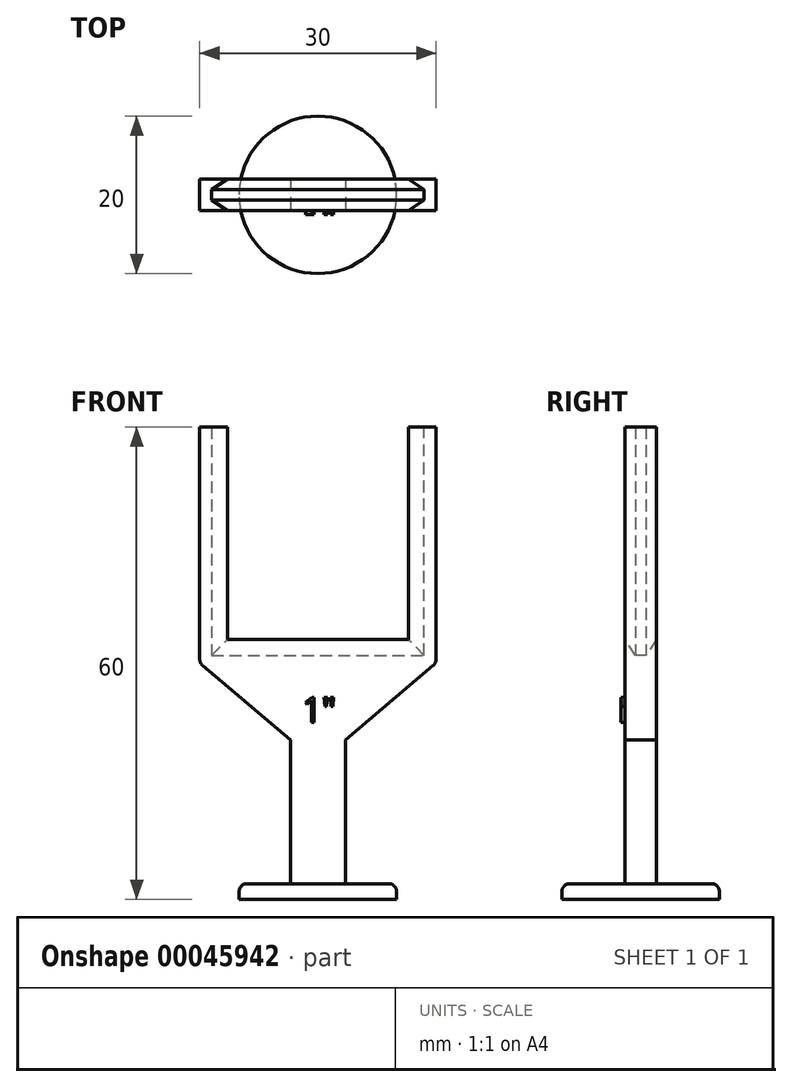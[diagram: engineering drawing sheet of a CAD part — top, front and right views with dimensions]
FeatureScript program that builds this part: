
annotation { "Feature Type Name" : "Feature", "Feature Type Description" : "" }
export const myFeature = defineFeature(function(context is Context, id is Id, definition is map)
    precondition{}
    {
        {
            var Q0;
            Q0=qCreatedBy(makeId("Top.planeOp"),FACE);
            var sketch = newSketch(context, id + "F0", { "sketchPlane" : qUnion([Q0])});
            skCircle(sketch, "E0", {"center": v(0, 0) * mm, "radius": 10 * mm});
            skSolve(sketch);
        }
        {
            var Q0;
            Q0=makeQuery(id+"F0.imprint","IMPRINT",FACE,{"disambiguationData":[TD([[makeQuery(id+"F0.imprint","IMPRINT",EDGE,{"derivedFrom":sQuery(id+"F0.wireOp",EDGE,"E0")}),1.0]])]});
            extrude(context, id + "F1", {"entities" : qUnion([Q0]), "depth" : 2 * mm});
        }
        {
            var Q0;
            Q0=qCreatedBy(makeId("Front.planeOp"),FACE);
            var sketch = newSketch(context, id + "F2", { "sketchPlane" : qUnion([Q0])});
            skLineSegment(sketch, "E1", {"start": v(0, 0) * mm, "end": v(0, 45) * mm, "construction": true});
            skLineSegment(sketch, "E2", {"start": v(-15, 45) * mm, "end": v(15, 45) * mm, "construction": true});
            skLineSegment(sketch, "E3", {"start": v(-3.5, 30) * mm, "end": v(3.5, 30) * mm, "construction": true});
            skLineSegment(sketch, "E4.0", {"start": v(-10, 2) * mm, "end": v(10, 2) * mm, "construction": true});
            skLineSegment(sketch, "E5", {"start": v(-3.5, 30) * mm, "end": v(-3.5, 2) * mm});
            skLineSegment(sketch, "E6.MirrorCS", {"start": v(3.5, 30) * mm, "end": v(3.5, 2) * mm});
            skLineSegment(sketch, "E7", {"start": v(-3.5, 2) * mm, "end": v(3.5, 2) * mm});
            skLineSegment(sketch, "E8.rect.bottom", {"start": v(15, 30) * mm, "end": v(-15, 30) * mm});
            skLineSegment(sketch, "E8.rect.top", {"start": v(15, 60) * mm, "end": v(-15, 60) * mm});
            skLineSegment(sketch, "E8.rect.left", {"start": v(15, 30) * mm, "end": v(15, 60) * mm});
            skLineSegment(sketch, "E8.rect.right", {"start": v(-15, 30) * mm, "end": v(-15, 60) * mm});
            skPoint(sketch, "E8.rect.middle", {"position": v(0, 45) * mm});
            skLineSegment(sketch, "E9.1", {"start": v(11.5, 33) * mm, "end": v(11.5, 60) * mm});
            skLineSegment(sketch, "E9.2", {"start": v(11.5, 33) * mm, "end": v(-11.5, 33) * mm});
            skLineSegment(sketch, "E9.3", {"start": v(-11.5, 33) * mm, "end": v(-11.5, 60) * mm});
            skLineSegment(sketch, "E10", {"start": v(0, 30) * mm, "end": v(0, 33) * mm, "construction": true});
            skLineSegment(sketch, "E11", {"start": v(0, 33) * mm, "end": v(-11.5, 33) * mm, "construction": true});
            skSolve(sketch);
        }
        {
            var Q0;
            {var subQ2=sQuery(id+"F2.wireOp",EDGE,"E5");Q0=makeQuery(id+"F2.imprint","IMPRINT",FACE,{"disambiguationData":[TD([[makeQuery(id+"F2.imprint","IMPRINT",EDGE,{"derivedFrom":subQ2}),1.0]])]});}
            var Q1;
            {var subQ0=sQuery(id+"F2.wireOp",EDGE,"E8.rect.left");Q1=makeQuery(id+"F2.imprint","IMPRINT",FACE,{"disambiguationData":[TD([[makeQuery(id+"F2.imprint","IMPRINT",EDGE,{"derivedFrom":subQ0}),1.0]])]});}
            extrude(context, id + "F3", {"entities" : qUnion([Q0, Q1]), "operationType" : NewBodyOperationType.ADD, "endBound" : BoundingType.SYMMETRIC, "depth" : 4 * mm, "hasSecondDirection" : true, "secondDirectionOppositeDirection" : true, "secondDirectionDepth" : 1.5 * mm});
        }
        {
            var Q0;
            Q0=makeQuery(id+"F3.opExtrude","CAP_VERTEX",VERTEX,{"disambiguationData":[OSD([sQuery(id+"F2.wireOp",EDGE,"E8.rect.top"),sQuery(id+"F2.wireOp",EDGE,"E9.3")])],"isStart":false});
            var Q1;
            Q1=makeQuery(id+"F3.opExtrude","CAP_EDGE",EDGE,{"disambiguationData":[OSD([sQuery(id+"F2.wireOp",EDGE,"E9.3")])],"isStart":false});
            cPlane(context, id + "F4", {"entities" : qUnion([Q0, Q1]), "cplaneType" : CPlaneType.CURVE_POINT, "offset" : 150 * mm, "width" : 150 * mm, "height" : 150 * mm});
        }
        {
            var Q0;
            Q0=qCreatedBy(id+"F4.planeOp",FACE);
            var sketch = newSketch(context, id + "F5", { "sketchPlane" : qUnion([Q0])});
            skLineSegment(sketch, "E12.0", {"start": v(-11.5, 2) * mm, "end": v(-11.5, -2) * mm});
            skLineSegment(sketch, "E13", {"start": v(-11.5, 0) * mm, "end": v(-13.5, 0) * mm, "construction": true});
            skLineSegment(sketch, "E14", {"start": v(-13.5, 0.65) * mm, "end": v(-13.5, -0.65) * mm});
            skLineSegment(sketch, "E15", {"start": v(-13.5, 0.65) * mm, "end": v(-11.5, 2) * mm});
            skLineSegment(sketch, "E16", {"start": v(-13.5, -0.65) * mm, "end": v(-11.5, -2) * mm});
            skSolve(sketch);
        }
        {
            var Q0;
            Q0=makeQuery(id+"F5.imprint","IMPRINT",FACE,{"disambiguationData":[TD([[makeQuery(id+"F5.imprint","IMPRINT",EDGE,{"derivedFrom":sQuery(id+"F5.wireOp",EDGE,"E12.0")}),-1.0]])]});
            var Q1;
            Q1=makeQuery(id+"F3.opExtrude","CAP_EDGE",EDGE,{"disambiguationData":[OSD([sQuery(id+"F2.wireOp",EDGE,"E9.3")])],"isStart":false});
            var Q2;
            Q2=makeQuery(id+"F3.opExtrude","CAP_EDGE",EDGE,{"disambiguationData":[OSD([sQuery(id+"F2.wireOp",EDGE,"E9.2")])],"isStart":false});
            var Q3;
            Q3=makeQuery(id+"F3.opExtrude","CAP_EDGE",EDGE,{"disambiguationData":[OSD([sQuery(id+"F2.wireOp",EDGE,"E9.1")])],"isStart":false});
            sweep(context, id + "F6", {"operationType" : NewBodyOperationType.REMOVE, "profiles" : qUnion([Q0]), "path" : qUnion([Q1, Q2, Q3])});
        }
        {
            var Q0;
            Q0=makeQuery(id+"F3.opExtrude","CAP_FACE",FACE,{"disambiguationData":[OSD([sQuery(id+"F2.wireOp",EDGE,"2eedeef1-0c84-48b1-a1d1-fd58b4077060"),sQuery(id+"F2.wireOp",EDGE,"c229b6c5-89b8-4870-855e-fcb2bb86a88d0.MirrorCS"),sQuery(id+"F2.wireOp",EDGE,"76dde04b-6d6e-49cb-a3f0-9f61c5932c53"),sQuery(id+"F2.wireOp",EDGE,"ccce22a9-8801-460d-b2e6-72a3cf553eda"),sQuery(id+"F2.wireOp",EDGE,"E5"),sQuery(id+"F2.wireOp",EDGE,"E6.MirrorCS"),sQuery(id+"F2.wireOp",EDGE,"E7")])],"isStart":false});
            var sketch = newSketch(context, id + "F7", { "sketchPlane" : qUnion([Q0])});
            skText(sketch, "E17", { "text": "1\"", "fontName": "OpenSans-Regular.ttf"});
            skPoint(sketch, "E18.1", {"position": v(0, 0) * mm});
            skLineSegment(sketch, "E19.0", {"start": v(0, 0) * mm, "end": v(0, 45) * mm, "construction": true});
            const initialGuessF7  = {"E17": [-0.002, 0.0225, 1, 0, 0.00317]};
            skSetInitialGuess(sketch, initialGuessF7);
            skSolve(sketch);
        }
        {
            var Q0;
            Q0=qSketchRegion(id+"F7",true);
            extrude(context, id + "F8", {"entities" : qUnion([Q0]), "operationType" : NewBodyOperationType.ADD, "depth" : .5 * mm});
        }
        {
            var Q0;
            Q0=makeQuery(id+"F3.opExtrude","CAP_FACE",FACE,{"disambiguationData":[OSD([sQuery(id+"F2.wireOp",EDGE,"E5"),sQuery(id+"F2.wireOp",EDGE,"E6.MirrorCS"),sQuery(id+"F2.wireOp",EDGE,"E7"),sQuery(id+"F2.wireOp",EDGE,"E8.rect.bottom"),sQuery(id+"F2.wireOp",EDGE,"E8.rect.top"),sQuery(id+"F2.wireOp",EDGE,"E8.rect.left"),sQuery(id+"F2.wireOp",EDGE,"E8.rect.right"),sQuery(id+"F2.wireOp",EDGE,"E9.1"),sQuery(id+"F2.wireOp",EDGE,"E9.2"),sQuery(id+"F2.wireOp",EDGE,"E9.3")])],"isStart":false});
            var sketch = newSketch(context, id + "F9", { "sketchPlane" : qUnion([Q0])});
            skLineSegment(sketch, "E20", {"start": v(-15, 30) * mm, "end": v(-3.5, 20.23) * mm});
            skLineSegment(sketch, "E21.MirrorCS", {"start": v(15, 30) * mm, "end": v(3.5, 20.23) * mm});
            skSolve(sketch);
        }
        {
            var Q0;
            {var subQ2=sQuery(id+"F9.wireOp",EDGE,"E20");Q0=makeQuery(id+"F9.imprint","IMPRINT",FACE,{"disambiguationData":[TD([[makeQuery(id+"F9.imprint","IMPRINT",EDGE,{"derivedFrom":subQ2}),1.0]])]});}
            var Q1;
            {var subQ2=sQuery(id+"F9.wireOp",EDGE,"E21.MirrorCS");Q1=makeQuery(id+"F9.imprint","IMPRINT",FACE,{"disambiguationData":[TD([[makeQuery(id+"F9.imprint","IMPRINT",EDGE,{"derivedFrom":subQ2}),-1.0]])]});}
            extrude(context, id + "F10", {"entities" : qUnion([Q0, Q1]), "operationType" : NewBodyOperationType.ADD, "oppositeDirection" : true, "depth" : 4 * mm});
        }
        {
            var Q0;
            {var subQ0=sQuery(id+"F2.wireOp",EDGE,"76dde04b-6d6e-49cb-a3f0-9f61c5932c53");Q0=makeQuery(id+"F3.opExtrude","SWEPT_FACE",FACE,{"disambiguationData":[OSD([subQ0]),TDD([makeQuery(id+"F2.imprint","IMPRINT",EDGE,{"disambiguationData":[TD([[makeQuery(id+"F2.imprint","INTERSECT",VERTEX,{"derivedFrom":[sQuery(id+"F2.wireOp",EDGE,"2eedeef1-0c84-48b1-a1d1-fd58b4077060"),subQ0]}),-1.0]])],"derivedFrom":subQ0})])]});}
            var Q1;
            {var subQ0=sQuery(id+"F2.wireOp",EDGE,"76dde04b-6d6e-49cb-a3f0-9f61c5932c53");Q1=makeQuery(id+"F3.opExtrude","SWEPT_FACE",FACE,{"disambiguationData":[OSD([subQ0]),TDD([makeQuery(id+"F2.imprint","IMPRINT",EDGE,{"disambiguationData":[TD([[makeQuery(id+"F2.imprint","INTERSECT",VERTEX,{"derivedFrom":[sQuery(id+"F2.wireOp",EDGE,"c229b6c5-89b8-4870-855e-fcb2bb86a88d0.MirrorCS"),subQ0]}),1.0]])],"derivedFrom":subQ0})])]});}
            var Q2;
            Q2=makeQuery(id+"F3.opExtrude","CAP_EDGE",EDGE,{"disambiguationData":[OSD([sQuery(id+"F2.wireOp",EDGE,"E7")])],"isStart":false});
            var Q3;
            Q3=makeQuery(id+"F1.opExtrude","CAP_EDGE",EDGE,{"disambiguationData":[OSD([sQuery(id+"F0.wireOp",EDGE,"E0")])],"isStart":false});
            var Q4;
            Q4=makeQuery(id+"F10.opExtrude","SWEPT_EDGE",EDGE,{"disambiguationData":[OSD([sQuery(id+"F2.wireOp",EDGE,"E5"),sQuery(id+"F9.wireOp",EDGE,"E20")])]});
            var Q5;
            {var subQ0=sQuery(id+"F2.wireOp",EDGE,"E8.rect.bottom");var subQ1=sQuery(id+"F2.wireOp",EDGE,"E8.rect.right");Q5=makeQuery(id+"F10.boolean.opBoolean","MERGE",EDGE,{"derivedFrom":[makeQuery(id+"F3.opExtrude","SWEPT_EDGE",EDGE,{"disambiguationData":[OSD([subQ0,subQ1])]}),makeQuery(id+"F10.opExtrude","SWEPT_EDGE",EDGE,{"disambiguationData":[OSD([subQ0,subQ1,sQuery(id+"F9.wireOp",EDGE,"E20")])]})]});}
            var Q6;
            {var subQ0=sQuery(id+"F2.wireOp",EDGE,"E8.rect.bottom");var subQ1=sQuery(id+"F2.wireOp",EDGE,"E8.rect.left");Q6=makeQuery(id+"F10.boolean.opBoolean","MERGE",EDGE,{"derivedFrom":[makeQuery(id+"F3.opExtrude","SWEPT_EDGE",EDGE,{"disambiguationData":[OSD([subQ0,subQ1])]}),makeQuery(id+"F10.opExtrude","SWEPT_EDGE",EDGE,{"disambiguationData":[OSD([subQ0,subQ1,sQuery(id+"F9.wireOp",EDGE,"E21.MirrorCS")])]})]});}
            var Q7;
            Q7=makeQuery(id+"F10.opExtrude","SWEPT_EDGE",EDGE,{"disambiguationData":[OSD([sQuery(id+"F2.wireOp",EDGE,"E6.MirrorCS"),sQuery(id+"F9.wireOp",EDGE,"E21.MirrorCS")])]});
            fillet(context, id + "F11", {"entities" : qUnion([Q0, Q1, Q2, Q3, Q4, Q5, Q6, Q7]), "radius" : 1 * mm, "tangentPropagation" : true, "allowEdgeOverflow" : false});
        }
    });
